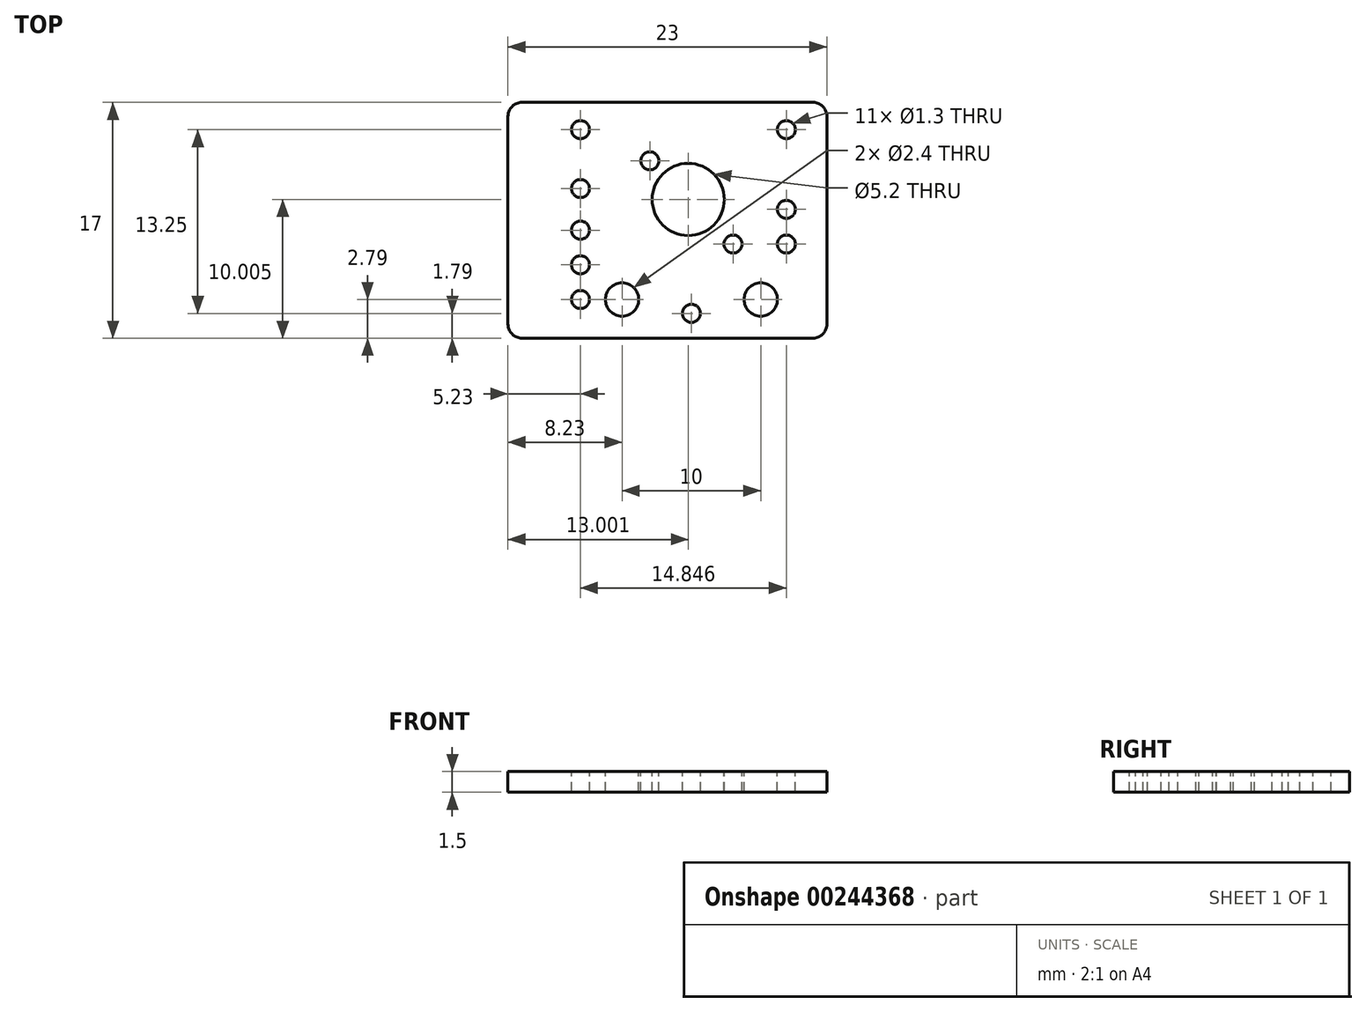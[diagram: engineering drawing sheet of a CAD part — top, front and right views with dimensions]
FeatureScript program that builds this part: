
annotation { "Feature Type Name" : "Feature", "Feature Type Description" : "" }
export const myFeature = defineFeature(function(context is Context, id is Id, definition is map)
    precondition{}
    {
        {
            var Q0;
            Q0=qCreatedBy(makeId("Top.planeOp"),FACE);
            var sketch = newSketch(context, id + "F0", { "sketchPlane" : qUnion([Q0])});
            skLineSegment(sketch, "E0", {"start": v(-12.23, 7.21) * mm, "end": v(8.77, 7.21) * mm});
            skLineSegment(sketch, "E1", {"start": v(9.77, 6.21) * mm, "end": v(9.77, -8.79) * mm});
            skLineSegment(sketch, "E2", {"start": v(8.77, -9.79) * mm, "end": v(-12.23, -9.79) * mm});
            skLineSegment(sketch, "E3", {"start": v(-13.23, -8.79) * mm, "end": v(-13.23, 6.21) * mm});
            skPoint(sketch, "E4.newPointA", {"position": v(-13.23, 7.73) * mm});
            skArc(sketch, "E4.filletArc", {"start": v(-12.23, 7.21) * mm, "mid": v(-12.94, 6.92) * mm, "end": v(-13.23, 6.21) * mm});
            skArc(sketch, "E5.filletArc", {"start": v(9.77, 6.21) * mm, "mid": v(9.48, 6.92) * mm, "end": v(8.77, 7.21) * mm});
            skArc(sketch, "E6.filletArc", {"start": v(8.77, -9.79) * mm, "mid": v(9.48, -9.5) * mm, "end": v(9.77, -8.79) * mm});
            skPoint(sketch, "E7.visualSharp", {"position": v(-13.23, -9.79) * mm});
            skArc(sketch, "E7.filletArc", {"start": v(-13.23, -8.79) * mm, "mid": v(-12.94, -9.5) * mm, "end": v(-12.23, -9.79) * mm});
            skSolve(sketch);
        }
        {
            var Q0;
            Q0 = qSketchRegion(id + "F0", true);
            extrude(context, id + "F1", {"entities" : qUnion([Q0]), "depth" : 1.5 * mm});
        }
        {
            var Q0;
            Q0=makeQuery(id+"F1.opExtrude","CAP_FACE",FACE,{"disambiguationData":[OSD([sQuery(id+"F0.wireOp",EDGE,"E0"),sQuery(id+"F0.wireOp",EDGE,"E1"),sQuery(id+"F0.wireOp",EDGE,"BHbmHS0J-i3Xx-4d6p-fsTU-bkkSeQT16j2F"),sQuery(id+"F0.wireOp",EDGE,"Pxyrazc0-ufuX-MaGq-Lisa-V6kmK2EmZJ5E")])],"isStart":false});
            var sketch = newSketch(context, id + "F2", { "sketchPlane" : qUnion([Q0])});
            skCircle(sketch, "E8", {"center": v(-0.23, 0.21) * mm, "radius": 2.6 * mm});
            skSolve(sketch);
        }
        {
            var Q0;
            Q0=makeQuery(id+"F1.opExtrude","CAP_FACE",FACE,{"disambiguationData":[OSD([sQuery(id+"F0.wireOp",EDGE,"0JzyJq7d-DXwQ-p0i9-ll30-icSSdf44xIEe"),sQuery(id+"F0.wireOp",EDGE,"E0"),sQuery(id+"F0.wireOp",EDGE,"E1")])],"isStart":false});
            var sketch = newSketch(context, id + "F3", { "sketchPlane" : qUnion([Q0])});
            skCircle(sketch, "E9", {"center": v(-5, -7) * mm, "radius": 1.2 * mm});
            skCircle(sketch, "E10.MirrorC", {"center": v(5, -7) * mm, "radius": 1.2 * mm});
            skSolve(sketch);
        }
        {
            var Q0;
            Q0 = qSketchRegion(id + "F3", true);
            extrude(context, id + "F4", {"entities" : qUnion([Q0]), "operationType" : NewBodyOperationType.REMOVE, "oppositeDirection" : true, "depth" : 4 * mm});
        }
        {
            var Q0;
            Q0=makeQuery(id+"F1.opExtrude","CAP_FACE",FACE,{"disambiguationData":[OSD([sQuery(id+"F0.wireOp",EDGE,"0JzyJq7d-DXwQ-p0i9-ll30-icSSdf44xIEe"),sQuery(id+"F0.wireOp",EDGE,"E0"),sQuery(id+"F0.wireOp",EDGE,"E1")])],"isStart":false});
            var sketch = newSketch(context, id + "F5", { "sketchPlane" : qUnion([Q0])});
            skCircle(sketch, "E11", {"center": v(-8, -7) * mm, "radius": 0.65 * mm});
            skCircle(sketch, "E12.1.0.0", {"center": v(-8, -4.5) * mm, "radius": 0.65 * mm});
            skCircle(sketch, "E12.2.0.0", {"center": v(-8, -2) * mm, "radius": 0.65 * mm});
            skLineSegment(sketch, "E12.direction1", {"start": v(-8, -7) * mm, "end": v(-8, -4.5) * mm, "construction": true});
            skCircle(sketch, "E13", {"center": v(0, -8) * mm, "radius": 0.65 * mm});
            skSolve(sketch);
        }
        {
            var Q0;
            Q0 = qSketchRegion(id + "F5", true);
            extrude(context, id + "F6", {"entities" : qUnion([Q0]), "operationType" : NewBodyOperationType.REMOVE, "oppositeDirection" : true, "depth" : 25 * mm});
        }
        {
            var Q0;
            Q0=makeQuery(id+"F1.opExtrude","CAP_FACE",FACE,{"disambiguationData":[OSD([sQuery(id+"F0.wireOp",EDGE,"0JzyJq7d-DXwQ-p0i9-ll30-icSSdf44xIEe"),sQuery(id+"F0.wireOp",EDGE,"E0"),sQuery(id+"F0.wireOp",EDGE,"E1")])],"isStart":false});
            var sketch = newSketch(context, id + "F7", { "sketchPlane" : qUnion([Q0])});
            skCircle(sketch, "E14", {"center": v(-2.5, -4) * mm, "radius": 0.65 * mm, "construction": true});
            skCircle(sketch, "E15.1.0.0", {"center": v(-2.5, -10.5) * mm, "radius": 0.65 * mm, "construction": true});
            skCircle(sketch, "E16.MirrorC", {"center": v(6.85, 5.25) * mm, "radius": 0.65 * mm});
            skCircle(sketch, "E17.MirrorC", {"center": v(6.85, -0.5) * mm, "radius": 0.65 * mm});
            skCircle(sketch, "E18", {"center": v(6.85, -3) * mm, "radius": 0.65 * mm});
            skSolve(sketch);
        }
        {
            var Q0;
            Q0 = qSketchRegion(id + "F7", true);
            extrude(context, id + "F8", {"entities" : qUnion([Q0]), "operationType" : NewBodyOperationType.REMOVE, "oppositeDirection" : true, "depth" : 25 * mm});
        }
        {
            var Q0;
            Q0=makeQuery(id+"F1.opExtrude","CAP_FACE",FACE,{"disambiguationData":[OSD([sQuery(id+"F0.wireOp",EDGE,"0JzyJq7d-DXwQ-p0i9-ll30-icSSdf44xIEe"),sQuery(id+"F0.wireOp",EDGE,"E0"),sQuery(id+"F0.wireOp",EDGE,"E1")])],"isStart":false});
            var sketch = newSketch(context, id + "F9", { "sketchPlane" : qUnion([Q0])});
            skCircle(sketch, "E19.0", {"center": v(-8, -2) * mm, "radius": 0.65 * mm, "construction": true});
            skCircle(sketch, "E20.0", {"center": v(-8, -7) * mm, "radius": 0.65 * mm, "construction": true});
            skCircle(sketch, "E21.MirrorC", {"center": v(-8, 5.25) * mm, "radius": 0.65 * mm});
            skCircle(sketch, "E22.MirrorC", {"center": v(-8, 1) * mm, "radius": 0.65 * mm});
            skSolve(sketch);
        }
        {
            var Q0;
            Q0 = qSketchRegion(id + "F9", true);
            var Q1;
            Q1=sQuery(id+"F9.wireOp",EDGE,"E19.0");
            var Q2;
            Q2=sQuery(id+"F9.wireOp",EDGE,"E20.0");
            extrude(context, id + "F10", {"entities" : qUnion([Q0]), "operationType" : NewBodyOperationType.REMOVE, "surfaceEntities" : qUnion([Q1, Q2]), "oppositeDirection" : true, "depth" : 25 * mm});
        }
        {
            var Q0;
            Q0=makeQuery(id+"F1.opExtrude","CAP_FACE",FACE,{"disambiguationData":[OSD([sQuery(id+"F0.wireOp",EDGE,"0JzyJq7d-DXwQ-p0i9-ll30-icSSdf44xIEe"),sQuery(id+"F0.wireOp",EDGE,"E0"),sQuery(id+"F0.wireOp",EDGE,"E1")])],"isStart":false});
            var sketch = newSketch(context, id + "F11", { "sketchPlane" : qUnion([Q0])});
            skCircle(sketch, "E23", {"center": v(3, -3) * mm, "radius": 0.65 * mm});
            skCircle(sketch, "E24.MirrorC", {"center": v(-3, 3) * mm, "radius": 0.65 * mm});
            skSolve(sketch);
        }
        {
            var Q0;
            Q0 = qSketchRegion(id + "F3", true);
            extrude(context, id + "F12", {"entities" : qUnion([Q0]), "operationType" : NewBodyOperationType.REMOVE, "oppositeDirection" : true, "depth" : 25 * mm});
        }
        {
            var Q0;
            Q0 = qSketchRegion(id + "F2", true);
            extrude(context, id + "F13", {"entities" : qUnion([Q0]), "operationType" : NewBodyOperationType.REMOVE, "oppositeDirection" : true, "depth" : 25 * mm});
        }
        {
            var Q0;
            Q0 = qSketchRegion(id + "F11", true);
            extrude(context, id + "F14", {"entities" : qUnion([Q0]), "operationType" : NewBodyOperationType.REMOVE, "oppositeDirection" : true, "depth" : 25 * mm});
        }
    });
